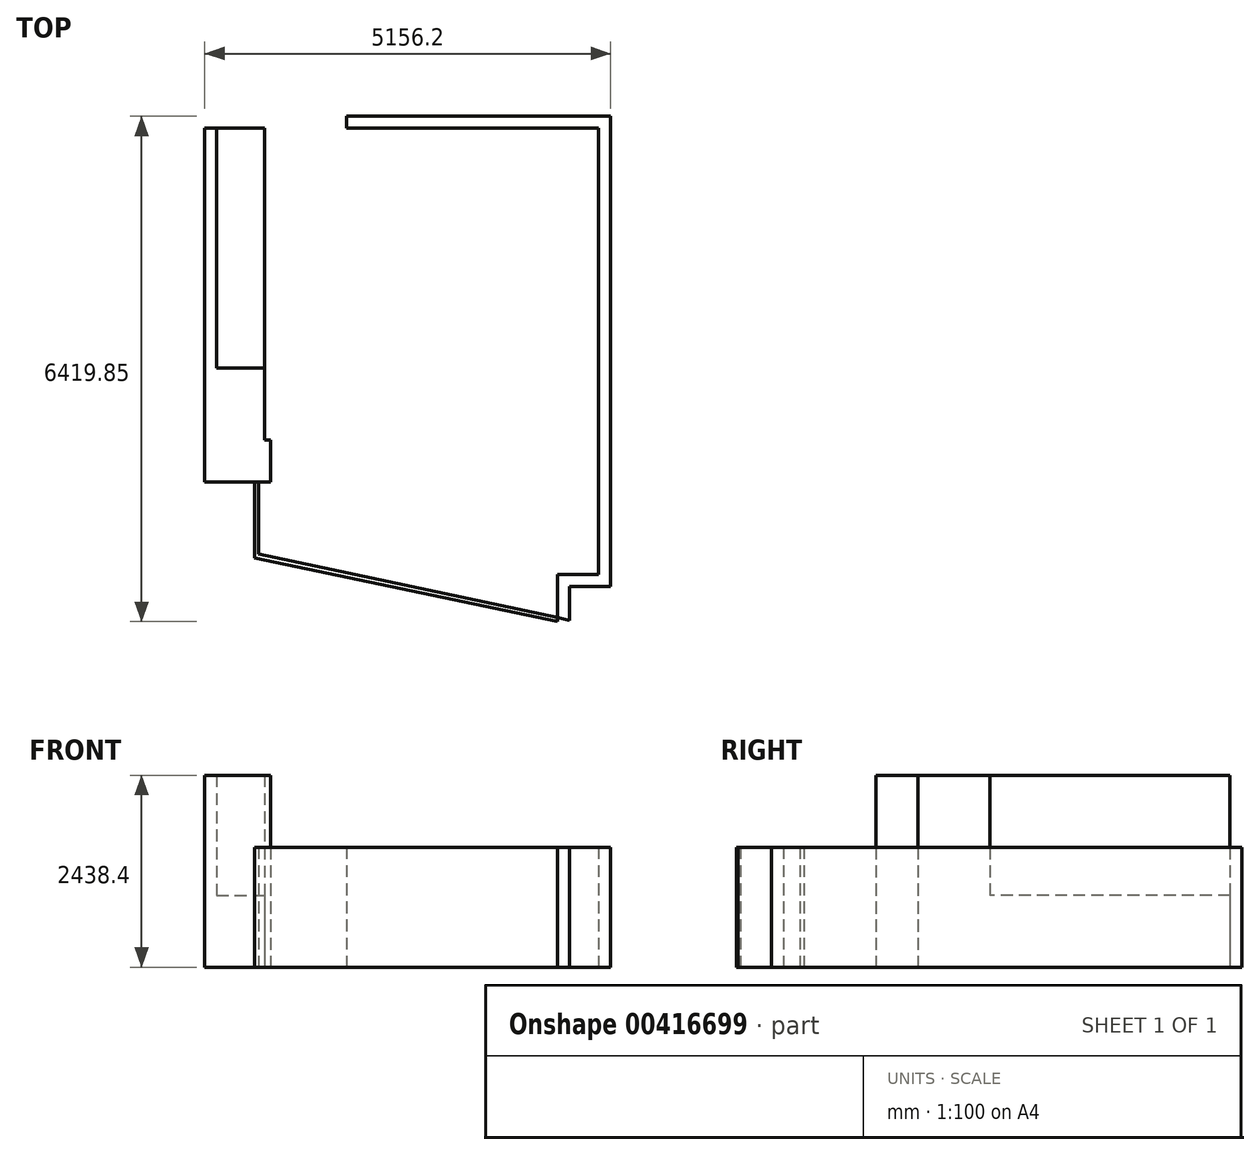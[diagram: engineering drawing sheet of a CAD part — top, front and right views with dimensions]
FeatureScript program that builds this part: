
annotation { "Feature Type Name" : "Feature", "Feature Type Description" : "" }
export const myFeature = defineFeature(function(context is Context, id is Id, definition is map)
    precondition{}
    {
        {
            var Q0;
            Q0=qCreatedBy(makeId("Top.planeOp"),FACE);
            var sketch = newSketch(context, id + "F0", { "sketchPlane" : qUnion([Q0])});
            skLineSegment(sketch, "E0", {"start": v(0, 0) * mm, "end": v(0, -3962.4) * mm});
            skLineSegment(sketch, "E1", {"start": v(0, -3962.4) * mm, "end": v(76.2, -3962.4) * mm});
            skLineSegment(sketch, "E2", {"start": v(76.2, -3962.4) * mm, "end": v(76.2, -4495.8) * mm});
            skLineSegment(sketch, "E3", {"start": v(76.2, -4495.8) * mm, "end": v(-76.2, -4495.8) * mm});
            skLineSegment(sketch, "E4", {"start": v(-76.2, -4495.8) * mm, "end": v(-76.2, -5410.2) * mm});
            skLineSegment(sketch, "E5", {"start": v(-76.2, -5410.2) * mm, "end": v(3721.1, -6216.65) * mm});
            skLineSegment(sketch, "E6", {"start": v(3721.1, -6216.65) * mm, "end": v(3721.1, -5670.55) * mm});
            skLineSegment(sketch, "E7", {"start": v(3721.1, -5670.55) * mm, "end": v(4241.8, -5670.55) * mm});
            skLineSegment(sketch, "E8", {"start": v(4241.8, -5670.55) * mm, "end": v(4241.8, 0) * mm});
            skLineSegment(sketch, "E9", {"start": v(4241.8, 0) * mm, "end": v(1041.4, 0) * mm});
            skLineSegment(sketch, "E10", {"start": v(1041.4, 0) * mm, "end": v(1041.4, 152.4) * mm});
            skLineSegment(sketch, "E11", {"start": v(1041.4, 152.4) * mm, "end": v(4394.2, 152.4) * mm});
            skLineSegment(sketch, "E12", {"start": v(4394.2, 152.4) * mm, "end": v(4394.2, -5822.95) * mm});
            skLineSegment(sketch, "E13", {"start": v(4394.2, -5822.95) * mm, "end": v(3873.5, -5822.95) * mm});
            skLineSegment(sketch, "E14", {"start": v(3873.5, -5822.95) * mm, "end": v(3873.5, -6249.02) * mm});
            skLineSegment(sketch, "E15", {"start": v(3873.5, -6249.02) * mm, "end": v(3721.1, -6216.65) * mm});
            skLineSegment(sketch, "E16", {"start": v(0, 0) * mm, "end": v(-609.6, 0) * mm});
            skLineSegment(sketch, "E17", {"start": v(-609.6, 0) * mm, "end": v(-762, 0) * mm});
            skLineSegment(sketch, "E18", {"start": v(-762, 0) * mm, "end": v(-762, -4495.8) * mm});
            skLineSegment(sketch, "E19", {"start": v(-609.6, 0) * mm, "end": v(-609.6, -3048) * mm});
            skLineSegment(sketch, "E20", {"start": v(-609.6, -3048) * mm, "end": v(0, -3048) * mm});
            skLineSegment(sketch, "E21", {"start": v(-762, -4495.8) * mm, "end": v(-76.2, -4495.8) * mm});
            skLineSegment(sketch, "E22", {"start": v(-127, -4495.8) * mm, "end": v(-127, -5461) * mm});
            skLineSegment(sketch, "E23", {"start": v(-127, -5461) * mm, "end": v(3721.1, -6267.45) * mm});
            skLineSegment(sketch, "E24", {"start": v(3721.1, -6267.45) * mm, "end": v(3721.1, -6216.65) * mm});
            skSolve(sketch);
        }
        {
            var Q0;
            {var subQ1=sQuery(id+"F0.wireOp",EDGE,"E1");Q0=makeQuery(id+"F0.imprint","IMPRINT",FACE,{"disambiguationData":[TD([[makeQuery(id+"F0.imprint","IMPRINT",EDGE,{"derivedFrom":subQ1}),-1.0]])]});}
            extrude(context, id + "F1", {"entities" : qUnion([Q0]), "depth" : 2438.4 * mm});
        }
        {
            var Q0;
            {var subQ2=sQuery(id+"F0.wireOp",EDGE,"E4");Q0=makeQuery(id+"F0.imprint","IMPRINT",FACE,{"disambiguationData":[TD([[makeQuery(id+"F0.imprint","IMPRINT",EDGE,{"derivedFrom":subQ2}),-1.0]])]});}
            extrude(context, id + "F2", {"entities" : qUnion([Q0]), "depth" : 1524 * mm});
        }
        {
            var Q0;
            {var subQ0=sQuery(id+"F0.wireOp",EDGE,"E16");Q0=makeQuery(id+"F0.imprint","IMPRINT",FACE,{"disambiguationData":[TD([[makeQuery(id+"F0.imprint","IMPRINT",EDGE,{"derivedFrom":subQ0}),1.0]])]});}
            extrude(context, id + "F3", {"entities" : qUnion([Q0]), "operationType" : NewBodyOperationType.ADD, "depth" : 914.4 * mm});
        }
        {
            var Q0;
            Q0=makeQuery(id+"F0.imprint","IMPRINT",FACE,{"disambiguationData":[TD([[makeQuery(id+"F0.imprint","IMPRINT",EDGE,{"derivedFrom":sQuery(id+"F0.wireOp",EDGE,"E6")}),-1.0]])]});
            extrude(context, id + "F4", {"entities" : qUnion([Q0]), "depth" : 1524 * mm});
        }
    });
